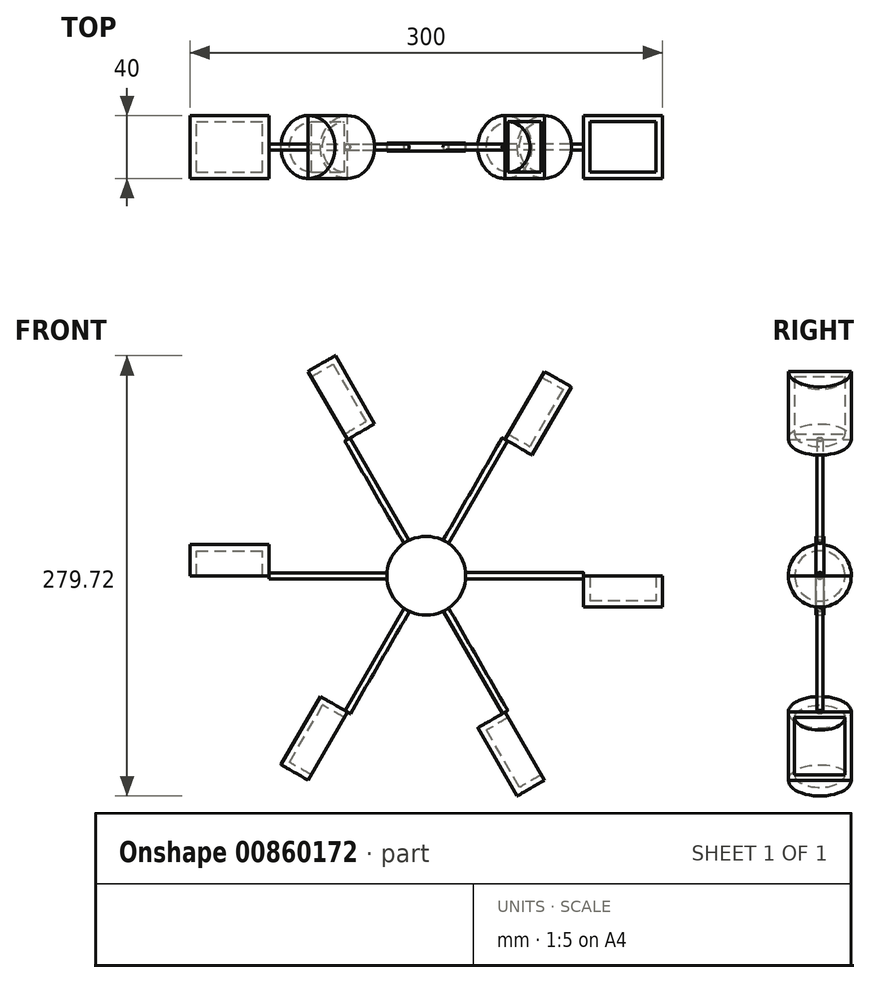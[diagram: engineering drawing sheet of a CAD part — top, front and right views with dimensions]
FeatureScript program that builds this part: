
annotation { "Feature Type Name" : "Feature", "Feature Type Description" : "" }
export const myFeature = defineFeature(function(context is Context, id is Id, definition is map)
    precondition{}
    {
        {
            var Q0;
            Q0=qCreatedBy(makeId("Front.planeOp"),FACE);
            var sketch = newSketch(context, id + "F0", { "sketchPlane" : qUnion([Q0])});
            skCircle(sketch, "E0", {"center": v(0, 0) * mm, "radius": 25 * mm});
            skSolve(sketch);
        }
        {
            var Q0;
            Q0 = qSketchRegion(id + "F0", true);
            extrude(context, id + "F1", {"entities" : qUnion([Q0]), "depth" : 5 * mm, "offsetDistance" : 25 * mm});
        }
        {
            var Q0;
            Q0=qCreatedBy(makeId("Right.planeOp"),FACE);
            var sketch = newSketch(context, id + "F2", { "sketchPlane" : qUnion([Q0])});
            skCircle(sketch, "E1", {"center": v(-2.55, 0.1) * mm, "radius": 1.96 * mm});
            skPoint(sketch, "E1.first.point", {"position": v(-0.6, 0) * mm});
            skPoint(sketch, "E1.second.point", {"position": v(-4.51, 0) * mm});
            skPoint(sketch, "E1.third.point", {"position": v(-4.02, 1.4) * mm});
            skSolve(sketch);
        }
        {
            var Q0;
            Q0 = qSketchRegion(id + "F2", true);
            extrude(context, id + "F3", {"entities" : qUnion([Q0]), "operationType" : NewBodyOperationType.ADD, "depth" : 100 * mm, "offsetDistance" : 25 * mm});
        }
        {
            var Q0;
            Q0=makeQuery(id+"F1.opExtrude","SWEPT_BODY",BODY,{"disambiguationData":[OSD([sQuery(id+"F0.wireOp",EDGE,"E0")])]});
            var Q1;
            Q1=makeQuery(id+"F1.opExtrude","SWEPT_FACE",FACE,{"disambiguationData":[OSD([sQuery(id+"F0.wireOp",EDGE,"E0")])]});
            circularPattern(context, id + "F4", {"entities" : qUnion([Q0]), "axis" : qUnion([Q1]), "angle" : 360 * degree, "instanceCount" : 6, "equalSpace" : true});
        }
        {
            var Q0;
            Q0=makeQuery(id+"F4.opPattern","COPY",FACE,{"derivedFrom":makeQuery(id+"F3.opExtrude","CAP_FACE",FACE,{"disambiguationData":[OSD([sQuery(id+"F2.wireOp",EDGE,"E1")])],"isStart":false}),"instanceName":"4"});
            var sketch = newSketch(context, id + "F5", { "sketchPlane" : qUnion([Q0])});
            skArc(sketch, "E2", {"start": v(0, -22.55) * mm, "mid": v(19.9, -2.55) * mm, "end": v(0, 17.45) * mm});
            skArc(sketch, "E3", {"start": v(0, -20.55) * mm, "mid": v(17.9, -2.55) * mm, "end": v(0, 15.45) * mm});
            skLineSegment(sketch, "E4", {"start": v(0, -22.55) * mm, "end": v(0, 17.45) * mm});
            skSolve(sketch);
        }
        {
            var Q0;
            Q0 = qSketchRegion(id + "F5", true);
            extrude(context, id + "F6", {"entities" : qUnion([Q0]), "depth" : 50 * mm, "offsetDistance" : 25 * mm});
        }
        {
            var Q0;
            Q0=makeQuery(id+"F6.opExtrude","SWEPT_FACE",FACE,{"disambiguationData":[OSD([sQuery(id+"F5.wireOp",EDGE,"E4")])]});
            shell(context, id + "F7", {"entities" : qUnion([Q0]), "thickness" : 4 * mm});
        }
        {
            var Q0;
            Q0=makeQuery(id+"F6.opExtrude","SWEPT_BODY",BODY,{"disambiguationData":[OSD([sQuery(id+"F5.wireOp",EDGE,"E2"),sQuery(id+"F5.wireOp",EDGE,"E4")])]});
            var Q1;
            Q1=makeQuery(id+"F1.opExtrude","SWEPT_FACE",FACE,{"disambiguationData":[OSD([sQuery(id+"F0.wireOp",EDGE,"E0")])]});
            circularPattern(context, id + "F8", {"entities" : qUnion([Q0]), "axis" : qUnion([Q1]), "angle" : 360 * degree, "instanceCount" : 6, "equalSpace" : true});
        }
    });
